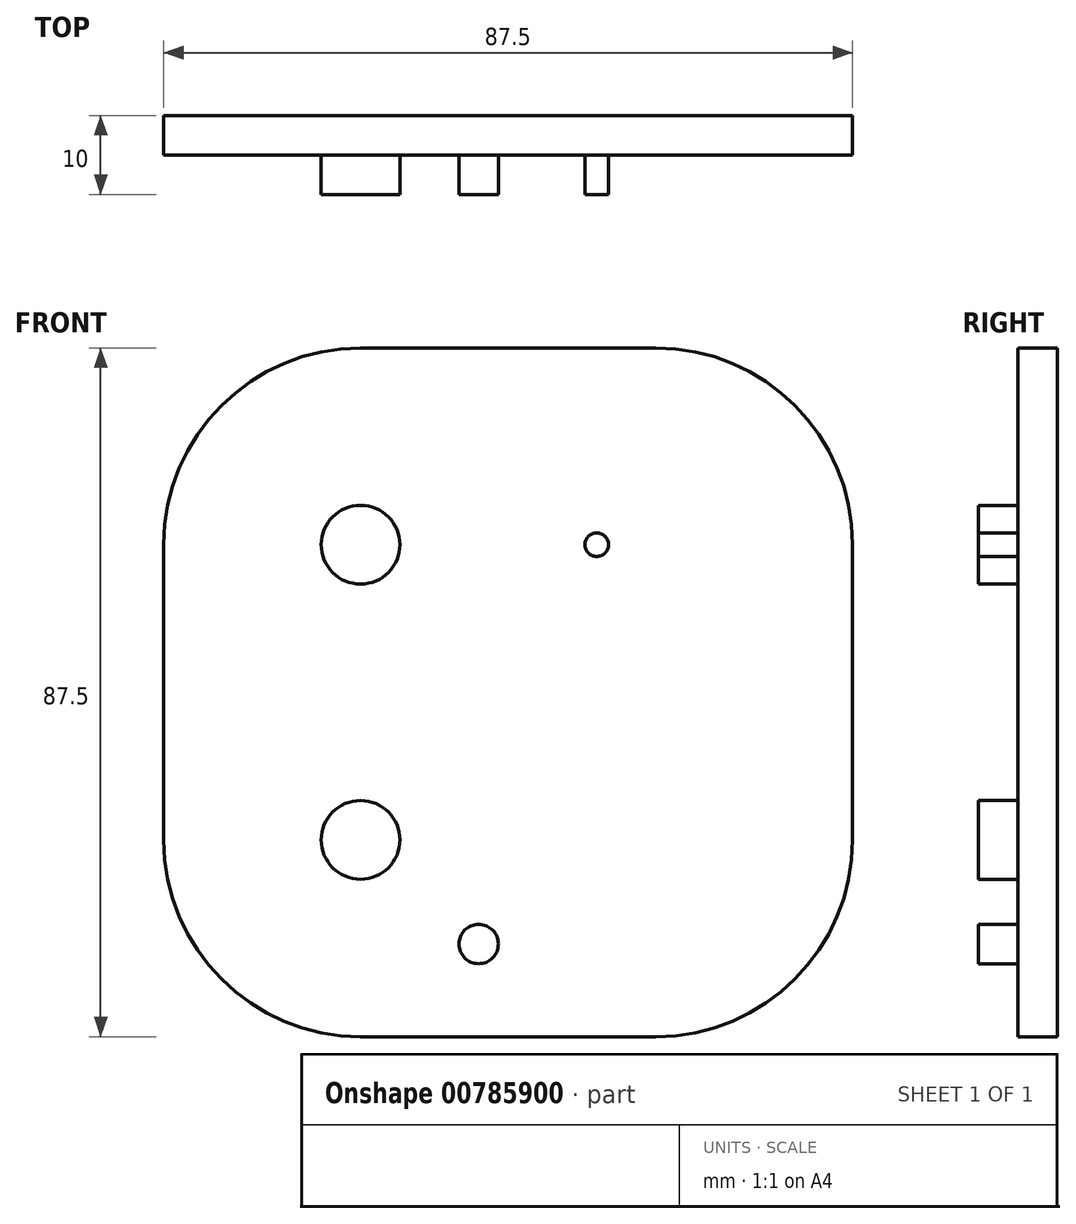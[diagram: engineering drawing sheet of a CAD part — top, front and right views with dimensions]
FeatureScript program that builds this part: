
annotation { "Feature Type Name" : "Feature", "Feature Type Description" : "" }
export const myFeature = defineFeature(function(context is Context, id is Id, definition is map)
    precondition{}
    {
        {
            var Q0;
            Q0=qCreatedBy(makeId("Front.planeOp"),FACE);
            var sketch = newSketch(context, id + "F0", { "sketchPlane" : qUnion([Q0])});
            skLineSegment(sketch, "E0.left", {"start": v(-25, 18.75) * mm, "end": v(-25, -18.75) * mm});
            skPoint(sketch, "E0.middle", {"position": v(0, 0) * mm});
            skArc(sketch, "E1", {"start": v(0, 43.75) * mm, "mid": v(-17.68, 36.43) * mm, "end": v(-25, 18.75) * mm});
            skArc(sketch, "E2", {"start": v(-25, -18.75) * mm, "mid": v(-17.68, -36.43) * mm, "end": v(0, -43.75) * mm});
            skLineSegment(sketch, "E3", {"start": v(0, 43.75) * mm, "end": v(37.5, 43.75) * mm});
            skLineSegment(sketch, "E4", {"start": v(0, -43.75) * mm, "end": v(37.5, -43.75) * mm});
            skLineSegment(sketch, "E5", {"start": v(62.5, 18.75) * mm, "end": v(62.5, -18.75) * mm});
            skPoint(sketch, "E6.visualSharp", {"position": v(62.5, 43.75) * mm});
            skArc(sketch, "E6.filletArc", {"start": v(62.5, 18.75) * mm, "mid": v(55.18, 36.43) * mm, "end": v(37.5, 43.75) * mm});
            skPoint(sketch, "E7.visualSharp", {"position": v(62.5, -43.75) * mm});
            skArc(sketch, "E7.filletArc", {"start": v(37.5, -43.75) * mm, "mid": v(55.18, -36.43) * mm, "end": v(62.5, -18.75) * mm});
            skPoint(sketch, "E8.orphan", {"position": v(25, -18.75) * mm});
            skSolve(sketch);
        }
        {
            var Q0;
            Q0 = qSketchRegion(id + "F0", true);
            extrude(context, id + "F1", {"entities" : qUnion([Q0]), "depth" : 5 * mm, "offsetDistance" : 25 * mm});
        }
        {
            var Q0;
            Q0=makeQuery(id+"F1.opExtrude","CAP_FACE",FACE,{"disambiguationData":[OSD([sQuery(id+"F0.wireOp",EDGE,"E0.left"),sQuery(id+"F0.wireOp",EDGE,"E0.right"),sQuery(id+"F0.wireOp",EDGE,"E1"),sQuery(id+"F0.wireOp",EDGE,"E2")])],"isStart":false});
            var sketch = newSketch(context, id + "F2", { "sketchPlane" : qUnion([Q0])});
            skCircle(sketch, "E9", {"center": v(0, 18.75) * mm, "radius": 5 * mm});
            skCircle(sketch, "E10", {"center": v(0, -18.75) * mm, "radius": 5 * mm});
            skCircle(sketch, "E11", {"center": v(15, -31.98) * mm, "radius": 2.5 * mm});
            skSolve(sketch);
        }
        {
            var Q0;
            Q0 = qSketchRegion(id + "F2", true);
            extrude(context, id + "F3", {"entities" : qUnion([Q0]), "operationType" : NewBodyOperationType.ADD, "depth" : 5 * mm, "offsetDistance" : 25 * mm});
        }
        {
            var Q0;
            Q0=makeQuery(id+"F1.opExtrude","CAP_FACE",FACE,{"disambiguationData":[OSD([sQuery(id+"F0.wireOp",EDGE,"E0.left"),sQuery(id+"F0.wireOp",EDGE,"E1"),sQuery(id+"F0.wireOp",EDGE,"E2"),sQuery(id+"F0.wireOp",EDGE,"E3"),sQuery(id+"F0.wireOp",EDGE,"E4"),sQuery(id+"F0.wireOp",EDGE,"E5"),sQuery(id+"F0.wireOp",EDGE,"E6.filletArc"),sQuery(id+"F0.wireOp",EDGE,"E7.filletArc")])],"isStart":false});
            var sketch = newSketch(context, id + "F4", { "sketchPlane" : qUnion([Q0])});
            skCircle(sketch, "E12", {"center": v(30, 18.75) * mm, "radius": 1.5 * mm});
            skSolve(sketch);
        }
        {
            var Q0;
            Q0 = qSketchRegion(id + "F4", true);
            extrude(context, id + "F5", {"entities" : qUnion([Q0]), "operationType" : NewBodyOperationType.ADD, "depth" : 5 * mm, "offsetDistance" : 25 * mm});
        }
    });
